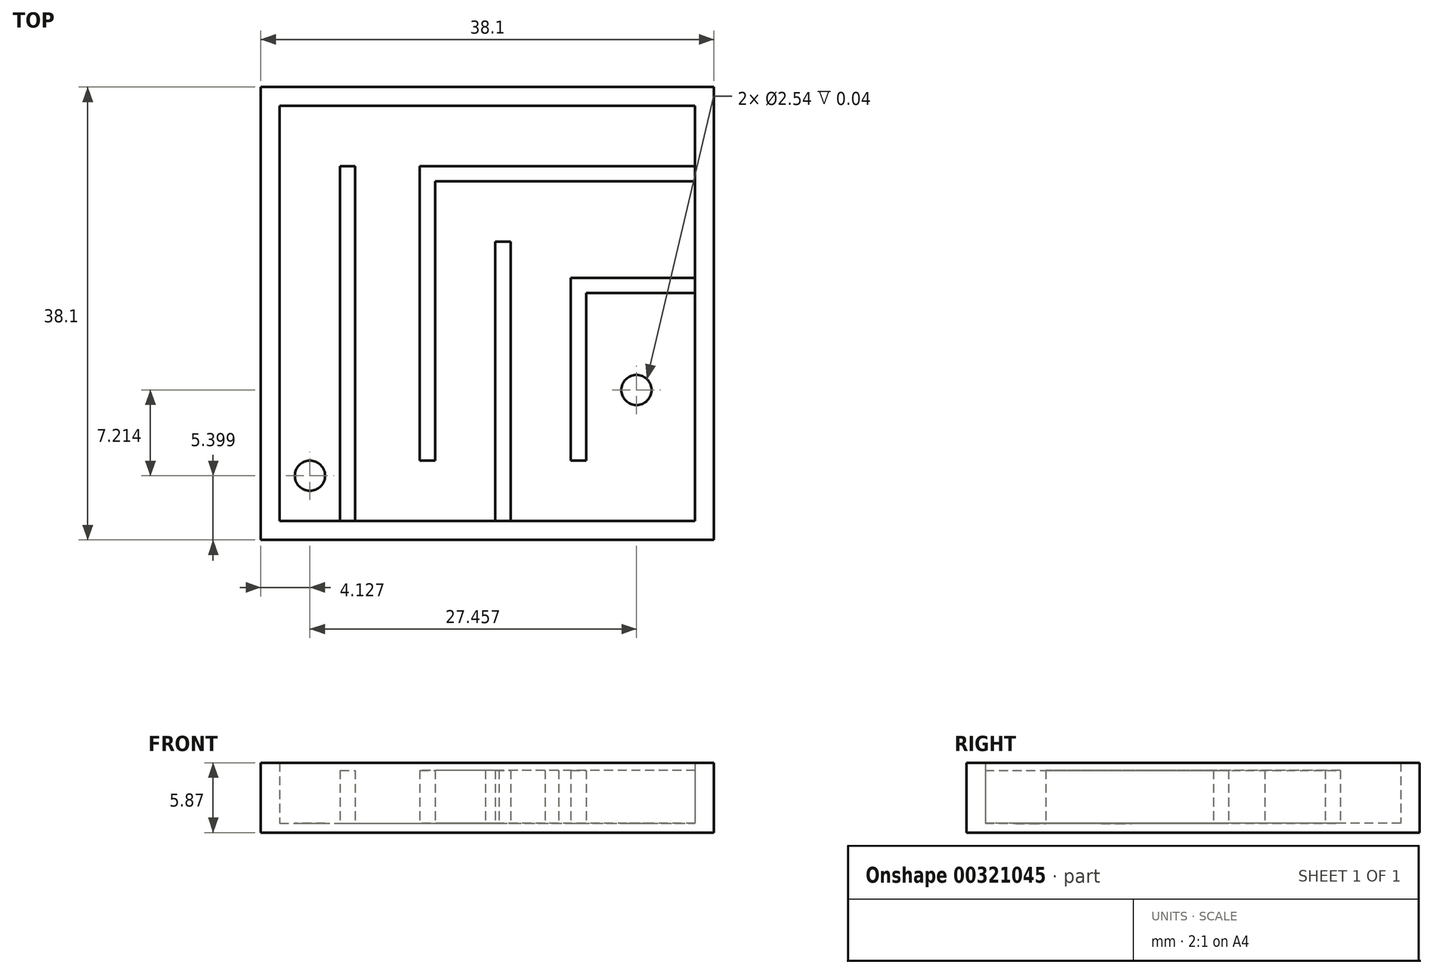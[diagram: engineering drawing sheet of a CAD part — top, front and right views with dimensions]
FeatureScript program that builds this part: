
annotation { "Feature Type Name" : "Feature", "Feature Type Description" : "" }
export const myFeature = defineFeature(function(context is Context, id is Id, definition is map)
    precondition{}
    {
        {
            var Q0;
            Q0=qCreatedBy(makeId("Top.planeOp"),FACE);
            var sketch = newSketch(context, id + "F0", { "sketchPlane" : qUnion([Q0])});
            skLineSegment(sketch, "E0.bottom", {"start": v(-16.91, 19.14) * mm, "end": v(21.19, 19.14) * mm});
            skLineSegment(sketch, "E0.top", {"start": v(-16.91, -18.96) * mm, "end": v(21.19, -18.96) * mm});
            skLineSegment(sketch, "E0.left", {"start": v(-16.91, 19.14) * mm, "end": v(-16.91, -18.96) * mm});
            skLineSegment(sketch, "E0.right", {"start": v(21.19, 19.14) * mm, "end": v(21.19, -18.96) * mm});
            skSolve(sketch);
        }
        {
            var Q0;
            Q0=makeQuery(id+"F0.imprint","IMPRINT",FACE,{"disambiguationData":[TD([[makeQuery(id+"F0.imprint","IMPRINT",EDGE,{"derivedFrom":sQuery(id+"F0.wireOp",EDGE,"E0.bottom")}),-1.0]])]});
            extrude(context, id + "F1", {"entities" : qUnion([Q0]), "depth" : 0.8 * mm});
        }
        {
            var Q0;
            Q0=makeQuery(id+"F1.opExtrude","CAP_FACE",FACE,{"disambiguationData":[OSD([sQuery(id+"F0.wireOp",EDGE,"E0.bottom"),sQuery(id+"F0.wireOp",EDGE,"E0.top"),sQuery(id+"F0.wireOp",EDGE,"E0.left"),sQuery(id+"F0.wireOp",EDGE,"E0.right")])],"isStart":false});
            var sketch = newSketch(context, id + "F2", { "sketchPlane" : qUnion([Q0])});
            skLineSegment(sketch, "E1.0", {"start": v(-15.32, 17.55) * mm, "end": v(19.6, 17.55) * mm});
            skLineSegment(sketch, "E1.1", {"start": v(-15.32, 17.55) * mm, "end": v(-15.32, -17.37) * mm});
            skLineSegment(sketch, "E1.2", {"start": v(-15.32, -17.37) * mm, "end": v(19.6, -17.37) * mm});
            skLineSegment(sketch, "E1.3", {"start": v(19.6, 17.55) * mm, "end": v(19.6, -17.37) * mm});
            skSolve(sketch);
        }
        {
            var Q0;
            Q0=makeQuery(id+"F2.imprint","IMPRINT",FACE,{"disambiguationData":[TD([[makeQuery(id+"F2.imprint","IMPRINT",EDGE,{"derivedFrom":sQuery(id+"F2.wireOp",EDGE,"E1.0")}),1.0]])]});
            extrude(context, id + "F3", {"entities" : qUnion([Q0]), "operationType" : NewBodyOperationType.ADD, "depth" : 5.08 * mm});
        }
        {
            var Q0;
            Q0=makeQuery(id+"F1.opExtrude","CAP_FACE",FACE,{"disambiguationData":[OSD([sQuery(id+"F0.wireOp",EDGE,"E0.bottom"),sQuery(id+"F0.wireOp",EDGE,"E0.top"),sQuery(id+"F0.wireOp",EDGE,"E0.left"),sQuery(id+"F0.wireOp",EDGE,"E0.right")])],"isStart":false});
            var sketch = newSketch(context, id + "F4", { "sketchPlane" : qUnion([Q0])});
            skLineSegment(sketch, "E2.bottom", {"start": v(-10.24, -17.37) * mm, "end": v(-8.97, -17.37) * mm});
            skLineSegment(sketch, "E2.top", {"start": v(-10.24, 12.47) * mm, "end": v(-8.97, 12.47) * mm});
            skLineSegment(sketch, "E2.left", {"start": v(-10.24, -17.37) * mm, "end": v(-10.24, 12.47) * mm});
            skLineSegment(sketch, "E2.right", {"start": v(-8.97, -17.37) * mm, "end": v(-8.97, 12.47) * mm});
            skLineSegment(sketch, "E3.bottom", {"start": v(19.6, 12.47) * mm, "end": v(-3.54, 12.47) * mm});
            skLineSegment(sketch, "E3.top", {"start": v(19.6, 11.2) * mm, "end": v(-2.27, 11.2) * mm});
            skLineSegment(sketch, "E3.left", {"start": v(19.6, 12.47) * mm, "end": v(19.6, 11.2) * mm});
            skLineSegment(sketch, "E3.right", {"start": v(-3.54, 12.47) * mm, "end": v(-3.54, 11.2) * mm});
            skLineSegment(sketch, "E4.bottom", {"start": v(-3.54, 12.47) * mm, "end": v(-2.27, 12.47) * mm});
            skLineSegment(sketch, "E4.top", {"start": v(-3.54, -12.3) * mm, "end": v(-2.27, -12.3) * mm});
            skLineSegment(sketch, "E4.left", {"start": v(-3.54, 12.47) * mm, "end": v(-3.54, -12.3) * mm});
            skLineSegment(sketch, "E4.right", {"start": v(-2.27, 11.2) * mm, "end": v(-2.27, -12.3) * mm});
            skLineSegment(sketch, "E5.bottom", {"start": v(2.81, -17.37) * mm, "end": v(4.08, -17.37) * mm});
            skLineSegment(sketch, "E5.top", {"start": v(2.81, 6.12) * mm, "end": v(4.08, 6.12) * mm});
            skLineSegment(sketch, "E5.left", {"start": v(2.81, -17.37) * mm, "end": v(2.81, 6.12) * mm});
            skLineSegment(sketch, "E5.right", {"start": v(4.08, -17.37) * mm, "end": v(4.08, 6.12) * mm});
            skLineSegment(sketch, "E6.bottom", {"start": v(19.6, 1.8) * mm, "end": v(10.43, 1.8) * mm});
            skLineSegment(sketch, "E6.top", {"start": v(19.6, 3.07) * mm, "end": v(9.16, 3.07) * mm});
            skLineSegment(sketch, "E6.left", {"start": v(19.6, 1.8) * mm, "end": v(19.6, 3.07) * mm});
            skLineSegment(sketch, "E6.right", {"start": v(9.16, 1.8) * mm, "end": v(9.16, 3.07) * mm});
            skLineSegment(sketch, "E7.bottom", {"start": v(9.16, 3.07) * mm, "end": v(10.43, 3.07) * mm});
            skLineSegment(sketch, "E7.top", {"start": v(9.16, -12.3) * mm, "end": v(10.43, -12.3) * mm});
            skLineSegment(sketch, "E7.left", {"start": v(9.16, 3.07) * mm, "end": v(9.16, -12.3) * mm});
            skLineSegment(sketch, "E7.right", {"start": v(10.43, 1.8) * mm, "end": v(10.43, -12.3) * mm});
            skText(sketch, "E8", { "text": "AAT", "fontName": "OpenSans-Bold.ttf"});
            const initialGuessF4  = {"E8": [0.00197, 0.01247, 1, 0, 0.00508]};
            skSetInitialGuess(sketch, initialGuessF4);
            skSolve(sketch);
        }
        {
            var Q0;
            Q0=makeQuery(id+"F4.imprint","IMPRINT",FACE,{"disambiguationData":[TD([[makeQuery(id+"F4.imprint","IMPRINT",EDGE,{"derivedFrom":sQuery(id+"F4.wireOp",EDGE,"E5.bottom")}),1.0]])]});
            var Q1;
            Q1=makeQuery(id+"F4.imprint","IMPRINT",FACE,{"disambiguationData":[TD([[makeQuery(id+"F4.imprint","IMPRINT",EDGE,{"derivedFrom":sQuery(id+"F4.wireOp",EDGE,"E6.bottom")}),-1.0]])]});
            var Q2;
            Q2=makeQuery(id+"F4.imprint","IMPRINT",FACE,{"disambiguationData":[TD([[makeQuery(id+"F4.imprint","IMPRINT",EDGE,{"derivedFrom":sQuery(id+"F4.wireOp",EDGE,"E3.top")}),-1.0]])]});
            var Q3;
            Q3=makeQuery(id+"F4.imprint","IMPRINT",FACE,{"disambiguationData":[TD([[makeQuery(id+"F4.imprint","IMPRINT",EDGE,{"derivedFrom":sQuery(id+"F4.wireOp",EDGE,"E2.bottom")}),1.0]])]});
            var Q4;
            Q4=makeQuery(id+"F4.imprint","IMPRINT",FACE,{"disambiguationData":[TD([[makeQuery(id+"F4.imprint","IMPRINT",EDGE,{"derivedFrom":sQuery(id+"F4.wireOp",EDGE,"E8.sketch_text.stroke-0")}),-1.0]])]});
            var Q5;
            Q5=makeQuery(id+"F4.imprint","IMPRINT",FACE,{"disambiguationData":[TD([[makeQuery(id+"F4.imprint","IMPRINT",EDGE,{"derivedFrom":sQuery(id+"F4.wireOp",EDGE,"E8.sketch_text.stroke-12")}),-1.0]])]});
            var Q6;
            Q6=makeQuery(id+"F4.imprint","IMPRINT",FACE,{"disambiguationData":[TD([[makeQuery(id+"F4.imprint","IMPRINT",EDGE,{"derivedFrom":sQuery(id+"F4.wireOp",EDGE,"E8.sketch_text.stroke-24")}),-1.0]])]});
            extrude(context, id + "F5", {"entities" : qUnion([Q0, Q1, Q2, Q3, Q4, Q5, Q6]), "operationType" : NewBodyOperationType.ADD, "depth" : 4.44 * mm});
        }
        {
            var Q0;
            Q0=makeQuery(id+"F5.boolean.opBoolean","SPLIT",FACE,{"disambiguationData":[TD([makeQuery(id+"F3.opExtrude","SWEPT_FACE",FACE,{"disambiguationData":[OSD([sQuery(id+"F2.wireOp",EDGE,"E1.0")])]})])],"derivedFrom":makeQuery(id+"F1.opExtrude","CAP_FACE",FACE,{"disambiguationData":[OSD([sQuery(id+"F0.wireOp",EDGE,"E0.bottom"),sQuery(id+"F0.wireOp",EDGE,"E0.top"),sQuery(id+"F0.wireOp",EDGE,"E0.left"),sQuery(id+"F0.wireOp",EDGE,"E0.right")])],"isStart":false})});
            var sketch = newSketch(context, id + "F6", { "sketchPlane" : qUnion([Q0])});
            skCircle(sketch, "E9", {"center": v(-12.78, -13.56) * mm, "radius": 1.27 * mm});
            skPoint(sketch, "E9.centerSnap0", {"position": v(-12.78, -17.37) * mm});
            skCircle(sketch, "E10", {"center": v(14.67, -6.35) * mm, "radius": 1.27 * mm});
            skSolve(sketch);
        }
        {
            var Q0;
            Q0=makeQuery(id+"F6.imprint","IMPRINT",FACE,{"disambiguationData":[TD([[makeQuery(id+"F6.imprint","IMPRINT",EDGE,{"derivedFrom":sQuery(id+"F6.wireOp",EDGE,"E9")}),1.0]])]});
            var Q1;
            Q1=makeQuery(id+"F6.imprint","IMPRINT",FACE,{"disambiguationData":[TD([[makeQuery(id+"F6.imprint","IMPRINT",EDGE,{"derivedFrom":sQuery(id+"F6.wireOp",EDGE,"E10")}),1.0]])]});
            extrude(context, id + "F7", {"entities" : qUnion([Q0, Q1]), "operationType" : NewBodyOperationType.REMOVE, "oppositeDirection" : true, "depth" : 0.04 * mm});
        }
    });
